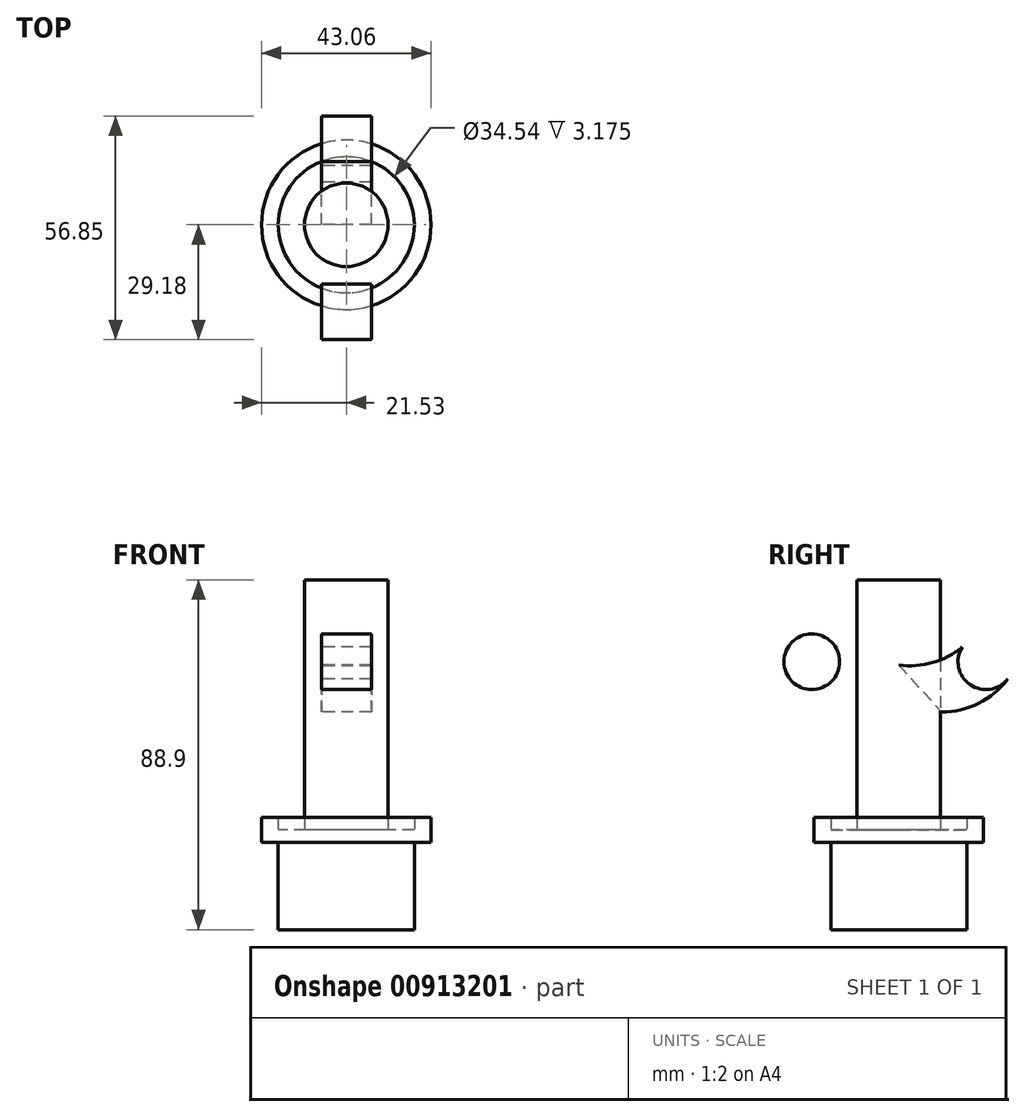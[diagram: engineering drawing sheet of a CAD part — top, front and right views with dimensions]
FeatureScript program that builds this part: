
annotation { "Feature Type Name" : "Feature", "Feature Type Description" : "" }
export const myFeature = defineFeature(function(context is Context, id is Id, definition is map)
    precondition{}
    {
        {
            var Q0;
            Q0=qCreatedBy(makeId("Top.planeOp"),FACE);
            var sketch = newSketch(context, id + "F0", { "sketchPlane" : qUnion([Q0])});
            skCircle(sketch, "E0", {"center": v(0, 0) * mm, "radius": 17.27 * mm});
            skCircle(sketch, "E1", {"center": v(0, 0) * mm, "radius": 21.53 * mm});
            skCircle(sketch, "E2", {"center": v(0, 0) * mm, "radius": 10.62 * mm});
            skSolve(sketch);
        }
        {
            var Q0;
            Q0=makeQuery(id+"F0.imprint","IMPRINT",FACE,{"disambiguationData":[TD([[makeQuery(id+"F0.imprint","IMPRINT",EDGE,{"derivedFrom":sQuery(id+"F0.wireOp",EDGE,"E0")}),-1.0]])]});
            extrude(context, id + "F1", {"entities" : qUnion([Q0]), "endBound" : BoundingType.SYMMETRIC, "depth" : 6.35 * mm, "offsetDistance" : 25.4 * mm});
        }
        {
            var Q0;
            Q0=makeQuery(id+"F0.imprint","IMPRINT",FACE,{"disambiguationData":[TD([[makeQuery(id+"F0.imprint","IMPRINT",EDGE,{"derivedFrom":sQuery(id+"F0.wireOp",EDGE,"E0")}),1.0]])]});
            extrude(context, id + "F2", {"entities" : qUnion([Q0]), "operationType" : NewBodyOperationType.ADD, "depth" : -25.4 * mm, "offsetDistance" : 25.4 * mm});
        }
        {
            var Q0;
            Q0=makeQuery(id+"F0.imprint","IMPRINT",FACE,{"disambiguationData":[TD([[makeQuery(id+"F0.imprint","IMPRINT",EDGE,{"derivedFrom":sQuery(id+"F0.wireOp",EDGE,"E2")}),1.0]])]});
            extrude(context, id + "F3", {"entities" : qUnion([Q0]), "operationType" : NewBodyOperationType.ADD, "endBound" : BoundingType.SYMMETRIC, "depth" : 50.8 * mm, "offsetDistance" : 25.4 * mm});
        }
        {
            var Q0;
            Q0=makeQuery(id+"F3.opExtrude","CAP_FACE",FACE,{"disambiguationData":[OSD([sQuery(id+"F0.wireOp",EDGE,"E2")])],"isStart":false});
            extrude(context, id + "F4", {"entities" : qUnion([Q0]), "operationType" : NewBodyOperationType.ADD, "depth" : 25.4 * mm, "offsetDistance" : 25.4 * mm});
        }
        {
            var Q0;
            Q0=qCreatedBy(makeId("Right.planeOp"),FACE);
            var sketch = newSketch(context, id + "F5", { "sketchPlane" : qUnion([Q0])});
            skLineSegment(sketch, "E3", {"start": v(0, 0) * mm, "end": v(21.2, 0) * mm});
            skLineSegment(sketch, "E4", {"start": v(21.2, 0) * mm, "end": v(0, 0) * mm});
            skLineSegment(sketch, "E5", {"start": v(0, 0) * mm, "end": v(-21.06, 0) * mm});
            skLineSegment(sketch, "E6", {"start": v(10.6, 0) * mm, "end": v(10.6, 29.88) * mm});
            skLineSegment(sketch, "E7", {"start": v(10.6, 29.88) * mm, "end": v(-10.83, 29.88) * mm});
            skArc(sketch, "E8", {"start": v(-10.83, 29.88) * mm, "mid": v(-20.25, 32.1) * mm, "end": v(-27.67, 38.3) * mm});
            skLineSegment(sketch, "E9", {"start": v(0, 0) * mm, "end": v(0, 29.88) * mm});
            skArc(sketch, "E10.MirrorCS", {"start": v(10.83, 29.88) * mm, "mid": v(20.25, 32.1) * mm, "end": v(27.67, 38.3) * mm});
            skCircle(sketch, "E11", {"center": v(-22.1, 42.66) * mm, "radius": 7.07 * mm});
            skArc(sketch, "E12", {"start": v(0.02, 41.83) * mm, "mid": v(-9.6, 42.78) * mm, "end": v(-17.8, 47.93) * mm});
            skArc(sketch, "E13.MirrorCS", {"start": v(-0.02, 41.83) * mm, "mid": v(9.6, 42.78) * mm, "end": v(17.8, 47.93) * mm});
            skCircle(sketch, "E14.MirrorC", {"center": v(22.1, 42.66) * mm, "radius": 7.07 * mm});
            skLineSegment(sketch, "E15", {"start": v(0, 29.88) * mm, "end": v(0.02, 41.83) * mm});
            skLineSegment(sketch, "E16", {"start": v(0.02, 41.83) * mm, "end": v(10.83, 29.88) * mm});
            skLineSegment(sketch, "E17", {"start": v(0.02, 41.83) * mm, "end": v(-10.83, 29.88) * mm});
            skLineSegment(sketch, "E18", {"start": v(10.83, 50.94) * mm, "end": v(-10.83, 50.94) * mm});
            skSolve(sketch);
        }
        {
            var Q0;
            {var subQ5=sQuery(id+"F5.wireOp",EDGE,"E8");Q0=makeQuery(id+"F5.imprint","IMPRINT",FACE,{"disambiguationData":[TD([[makeQuery(id+"F5.imprint","IMPRINT",EDGE,{"derivedFrom":subQ5}),-1.0]])]});}
            var Q1;
            {var subQ0=sQuery(id+"F5.wireOp",EDGE,"E10.MirrorCS");Q1=makeQuery(id+"F5.imprint","IMPRINT",FACE,{"disambiguationData":[TD([[makeQuery(id+"F5.imprint","IMPRINT",EDGE,{"derivedFrom":subQ0}),1.0]])]});}
            var Q2;
            {var subQ0=sQuery(id+"F5.wireOp",EDGE,"E14.MirrorC");var subQ1=makeQuery(id+"F5.imprint","INTERSECT",VERTEX,{"derivedFrom":[sQuery(id+"F5.wireOp",EDGE,"E10.MirrorCS"),subQ0]});Q2=makeQuery(id+"F5.imprint","IMPRINT",FACE,{"disambiguationData":[TD([[makeQuery(id+"F5.imprint","IMPRINT",EDGE,{"disambiguationData":[TD([[subQ1,1.0]])],"derivedFrom":subQ0}),-1.0]])]});}
            var Q3;
            {var subQ0=sQuery(id+"F5.wireOp",EDGE,"E11");var subQ1=makeQuery(id+"F5.imprint","INTERSECT",VERTEX,{"derivedFrom":[sQuery(id+"F5.wireOp",EDGE,"E8"),subQ0]});Q3=makeQuery(id+"F5.imprint","IMPRINT",FACE,{"disambiguationData":[TD([[makeQuery(id+"F5.imprint","IMPRINT",EDGE,{"disambiguationData":[TD([[subQ1,1.0]])],"derivedFrom":subQ0}),1.0]])]});}
            extrude(context, id + "F6", {"entities" : qUnion([Q0, Q1, Q2, Q3]), "endBound" : BoundingType.SYMMETRIC, "depth" : 12.7 * mm, "offsetDistance" : 25.4 * mm});
        }
        {
            var Q0;
            Q0=makeQuery(id+"F4.opExtrude","CAP_FACE",FACE,{"disambiguationData":[OSD([sQuery(id+"F0.wireOp",EDGE,"E2")])],"isStart":false});
            extrude(context, id + "F7", {"entities" : qUnion([Q0]), "operationType" : NewBodyOperationType.ADD, "depth" : 12.7 * mm, "offsetDistance" : 25.4 * mm});
        }
    });
